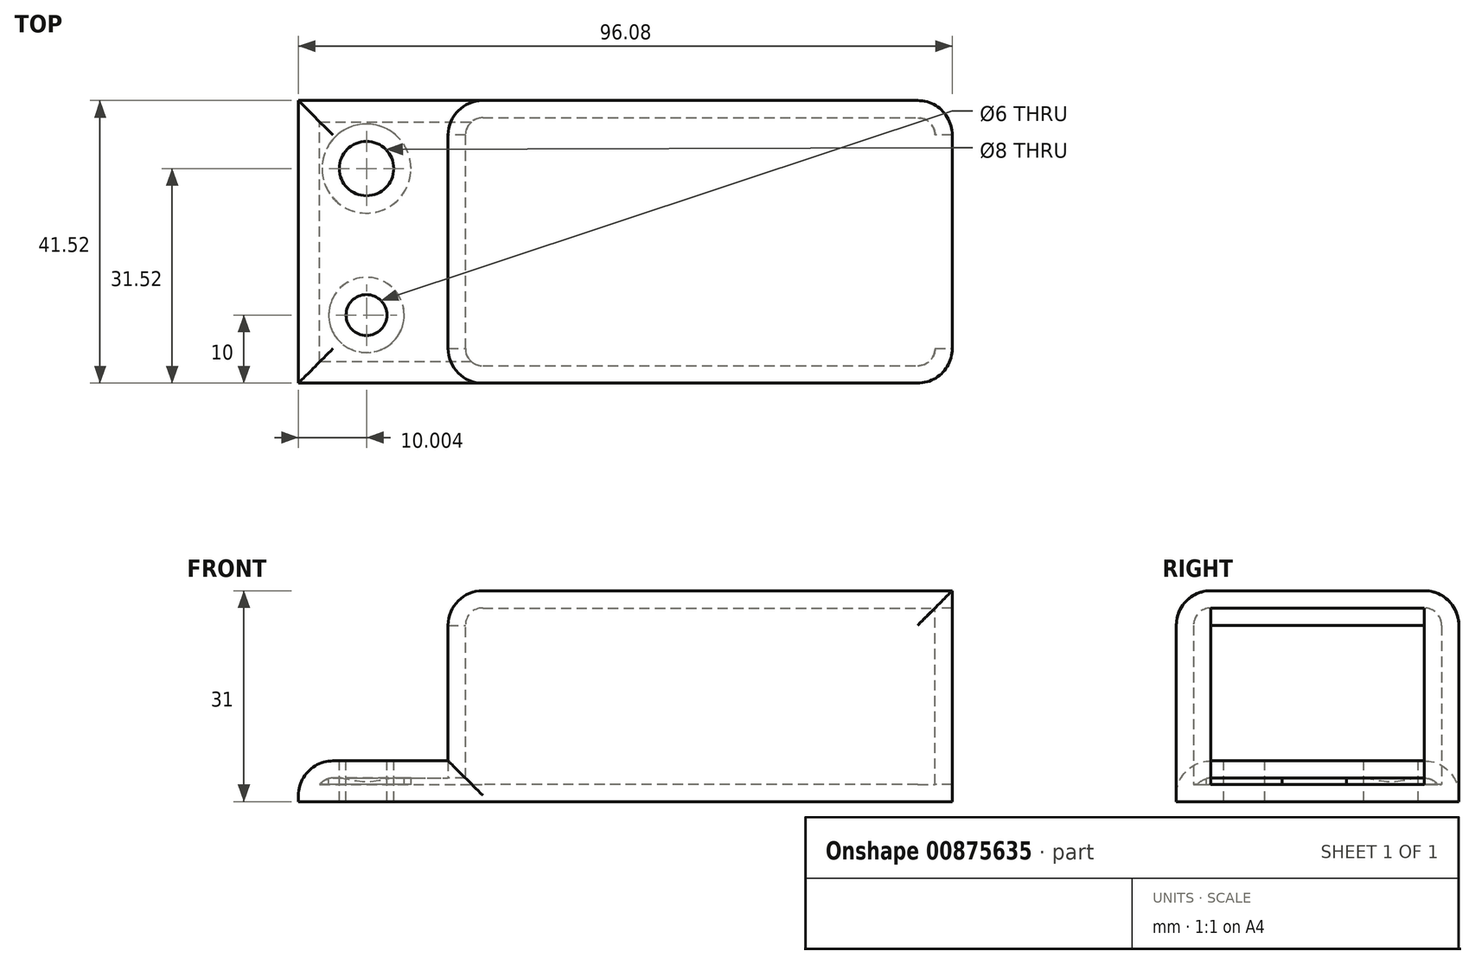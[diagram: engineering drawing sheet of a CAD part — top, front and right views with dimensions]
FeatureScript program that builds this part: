
annotation { "Feature Type Name" : "Feature", "Feature Type Description" : "" }
export const myFeature = defineFeature(function(context is Context, id is Id, definition is map)
    precondition{}
    {
        {
            var Q0;
            Q0=qCreatedBy(makeId("Top.planeOp"),FACE);
            var sketch = newSketch(context, id + "F0", { "sketchPlane" : qUnion([Q0])});
            skLineSegment(sketch, "E0.bottom", {"start": v(48.04, 20.76) * mm, "end": v(-48.04, 20.76) * mm});
            skLineSegment(sketch, "E0.top", {"start": v(48.04, -20.76) * mm, "end": v(-48.04, -20.76) * mm});
            skLineSegment(sketch, "E0.left", {"start": v(48.04, 20.76) * mm, "end": v(48.04, -20.76) * mm});
            skLineSegment(sketch, "E0.right", {"start": v(-48.04, 20.76) * mm, "end": v(-48.04, -20.76) * mm});
            skPoint(sketch, "E0.middle", {"position": v(0, 0) * mm});
            skSolve(sketch);
        }
        {
            var Q0;
            Q0 = qSketchRegion(id + "F0", true);
            extrude(context, id + "F1", {"entities" : qUnion([Q0]), "depth" : 6 * mm, "offsetDistance" : 25.4 * mm});
        }
        {
            var Q0;
            Q0=makeQuery(id+"F1.opExtrude","CAP_FACE",FACE,{"disambiguationData":[OSD([sQuery(id+"F0.wireOp",EDGE,"E0.bottom"),sQuery(id+"F0.wireOp",EDGE,"E0.top"),sQuery(id+"F0.wireOp",EDGE,"E0.left"),sQuery(id+"F0.wireOp",EDGE,"E0.right")])],"isStart":false});
            var sketch = newSketch(context, id + "F2", { "sketchPlane" : qUnion([Q0])});
            skCircle(sketch, "E1", {"center": v(-38.04, 10.76) * mm, "radius": 4.5 * mm});
            skCircle(sketch, "E2", {"center": v(-38.04, -10.76) * mm, "radius": 4 * mm});
            skLineSegment(sketch, "E3.bottom", {"start": v(48.04, 20.76) * mm, "end": v(-26.04, 20.76) * mm});
            skLineSegment(sketch, "E3.top", {"start": v(48.04, -20.76) * mm, "end": v(-26.04, -20.76) * mm});
            skLineSegment(sketch, "E3.left", {"start": v(48.04, 20.76) * mm, "end": v(48.04, -20.76) * mm});
            skLineSegment(sketch, "E3.right", {"start": v(-26.04, 20.76) * mm, "end": v(-26.04, -20.76) * mm});
            skSolve(sketch);
        }
        {
            var Q0;
            Q0=makeQuery(id+"F2.imprint","IMPRINT",FACE,{"disambiguationData":[TD([[makeQuery(id+"F2.imprint","IMPRINT",EDGE,{"derivedFrom":sQuery(id+"F2.wireOp",EDGE,"E3.bottom")}),1.0]])]});
            extrude(context, id + "F3", {"entities" : qUnion([Q0]), "operationType" : NewBodyOperationType.ADD, "depth" : 25 * mm, "offsetDistance" : 25.4 * mm});
        }
        {
            var Q0;
            Q0=sQuery(id+"F2.wireOp",VERTEX,"E2.center");
            var Q1;
            Q1=makeQuery(id+"F1.opExtrude","SWEPT_BODY",BODY,{"disambiguationData":[OSD([sQuery(id+"F0.wireOp",EDGE,"E0.bottom"),sQuery(id+"F0.wireOp",EDGE,"E0.top"),sQuery(id+"F0.wireOp",EDGE,"E0.left"),sQuery(id+"F0.wireOp",EDGE,"E0.right")])]});
            hole(context, id + "F4", {"style" : HoleStyle.SIMPLE, "endStyle" : HoleEndStyle.THROUGH, "holeDiameter" : 6 * mm, "majorDiameter" : 6.35 * mm, "isTappedThrough" : true, "tappedDepth" : 12.7 * mm, "tapClearance" : 3, "locations" : qUnion([Q0]), "scope" : qUnion([Q1])});
        }
        {
            var Q0;
            Q0=sQuery(id+"F2.wireOp",VERTEX,"E1.center");
            var Q1;
            Q1=makeQuery(id+"F1.opExtrude","SWEPT_BODY",BODY,{"disambiguationData":[OSD([sQuery(id+"F0.wireOp",EDGE,"E0.bottom"),sQuery(id+"F0.wireOp",EDGE,"E0.top"),sQuery(id+"F0.wireOp",EDGE,"E0.left"),sQuery(id+"F0.wireOp",EDGE,"E0.right")])]});
            hole(context, id + "F5", {"style" : HoleStyle.SIMPLE, "endStyle" : HoleEndStyle.THROUGH, "holeDiameter" : 8 * mm, "majorDiameter" : 6.35 * mm, "isTappedThrough" : true, "tappedDepth" : 12.7 * mm, "tapClearance" : 3, "locations" : qUnion([Q0]), "scope" : qUnion([Q1])});
        }
        {
            var Q0;
            Q0=makeQuery(id+"F3.opExtrude","CAP_EDGE",EDGE,{"disambiguationData":[OSD([sQuery(id+"F2.wireOp",EDGE,"E3.right")])],"isStart":false});
            var Q1;
            Q1=makeQuery(id+"F3.opExtrude","SWEPT_EDGE",EDGE,{"disambiguationData":[OSD([sQuery(id+"F0.wireOp",EDGE,"E0.top"),sQuery(id+"F2.wireOp",EDGE,"E3.top"),sQuery(id+"F2.wireOp",EDGE,"E3.right")])]});
            var Q2;
            Q2=makeQuery(id+"F1.opExtrude","CAP_EDGE",EDGE,{"disambiguationData":[OSD([sQuery(id+"F0.wireOp",EDGE,"E0.top")])],"isStart":false});
            var Q3;
            Q3=makeQuery(id+"F1.opExtrude","CAP_EDGE",EDGE,{"disambiguationData":[OSD([sQuery(id+"F0.wireOp",EDGE,"E0.right")])],"isStart":false});
            var Q4;
            Q4=makeQuery(id+"F1.opExtrude","CAP_EDGE",EDGE,{"disambiguationData":[OSD([sQuery(id+"F0.wireOp",EDGE,"E0.bottom")])],"isStart":false});
            var Q5;
            Q5=makeQuery(id+"F3.opExtrude","SWEPT_EDGE",EDGE,{"disambiguationData":[OSD([sQuery(id+"F0.wireOp",EDGE,"E0.bottom"),sQuery(id+"F2.wireOp",EDGE,"E3.bottom"),sQuery(id+"F2.wireOp",EDGE,"E3.right")])]});
            var Q6;
            Q6=makeQuery(id+"F3.opExtrude","CAP_EDGE",EDGE,{"disambiguationData":[OSD([sQuery(id+"F2.wireOp",EDGE,"E3.top")])],"isStart":false});
            var Q7;
            Q7=makeQuery(id+"F3.opExtrude","CAP_EDGE",EDGE,{"disambiguationData":[OSD([sQuery(id+"F2.wireOp",EDGE,"E3.bottom")])],"isStart":false});
            var Q8;
            Q8=makeQuery(id+"F3.boolean.opBoolean","MERGE",EDGE,{"derivedFrom":[makeQuery(id+"F1.opExtrude","SWEPT_EDGE",EDGE,{"disambiguationData":[OSD([sQuery(id+"F0.wireOp",EDGE,"E0.bottom"),sQuery(id+"F0.wireOp",EDGE,"E0.left")])]}),makeQuery(id+"F3.opExtrude","SWEPT_EDGE",EDGE,{"disambiguationData":[OSD([sQuery(id+"F2.wireOp",EDGE,"E3.bottom"),sQuery(id+"F2.wireOp",EDGE,"E3.left")])]})]});
            var Q9;
            Q9=makeQuery(id+"F3.boolean.opBoolean","MERGE",EDGE,{"derivedFrom":[makeQuery(id+"F1.opExtrude","SWEPT_EDGE",EDGE,{"disambiguationData":[OSD([sQuery(id+"F0.wireOp",EDGE,"E0.top"),sQuery(id+"F0.wireOp",EDGE,"E0.left")])]}),makeQuery(id+"F3.opExtrude","SWEPT_EDGE",EDGE,{"disambiguationData":[OSD([sQuery(id+"F2.wireOp",EDGE,"E3.top"),sQuery(id+"F2.wireOp",EDGE,"E3.left")])]})]});
            fillet(context, id + "F6", {"entities" : qUnion([Q0, Q1, Q2, Q3, Q4, Q5, Q6, Q7, Q8, Q9]), "radius" : 5.08 * mm, "tangentPropagation" : true, "allowEdgeOverflow" : false});
        }
        {
            var Q0;
            Q0=makeQuery(id+"F3.boolean.opBoolean","MERGE",FACE,{"derivedFrom":[makeQuery(id+"F1.opExtrude","SWEPT_FACE",FACE,{"disambiguationData":[OSD([sQuery(id+"F0.wireOp",EDGE,"E0.left")])]}),makeQuery(id+"F3.opExtrude","SWEPT_FACE",FACE,{"disambiguationData":[OSD([sQuery(id+"F2.wireOp",EDGE,"E3.left")])]})]});
            var Q1;
            Q1=makeQuery(id+"F3.opExtrude","SWEPT_FACE",FACE,{"disambiguationData":[OSD([sQuery(id+"F2.wireOp",EDGE,"E3.right")])]});
            shell(context, id + "F7", {"entities" : qUnion([Q0, Q1]), "thickness" : 2.54 * mm});
        }
    });
